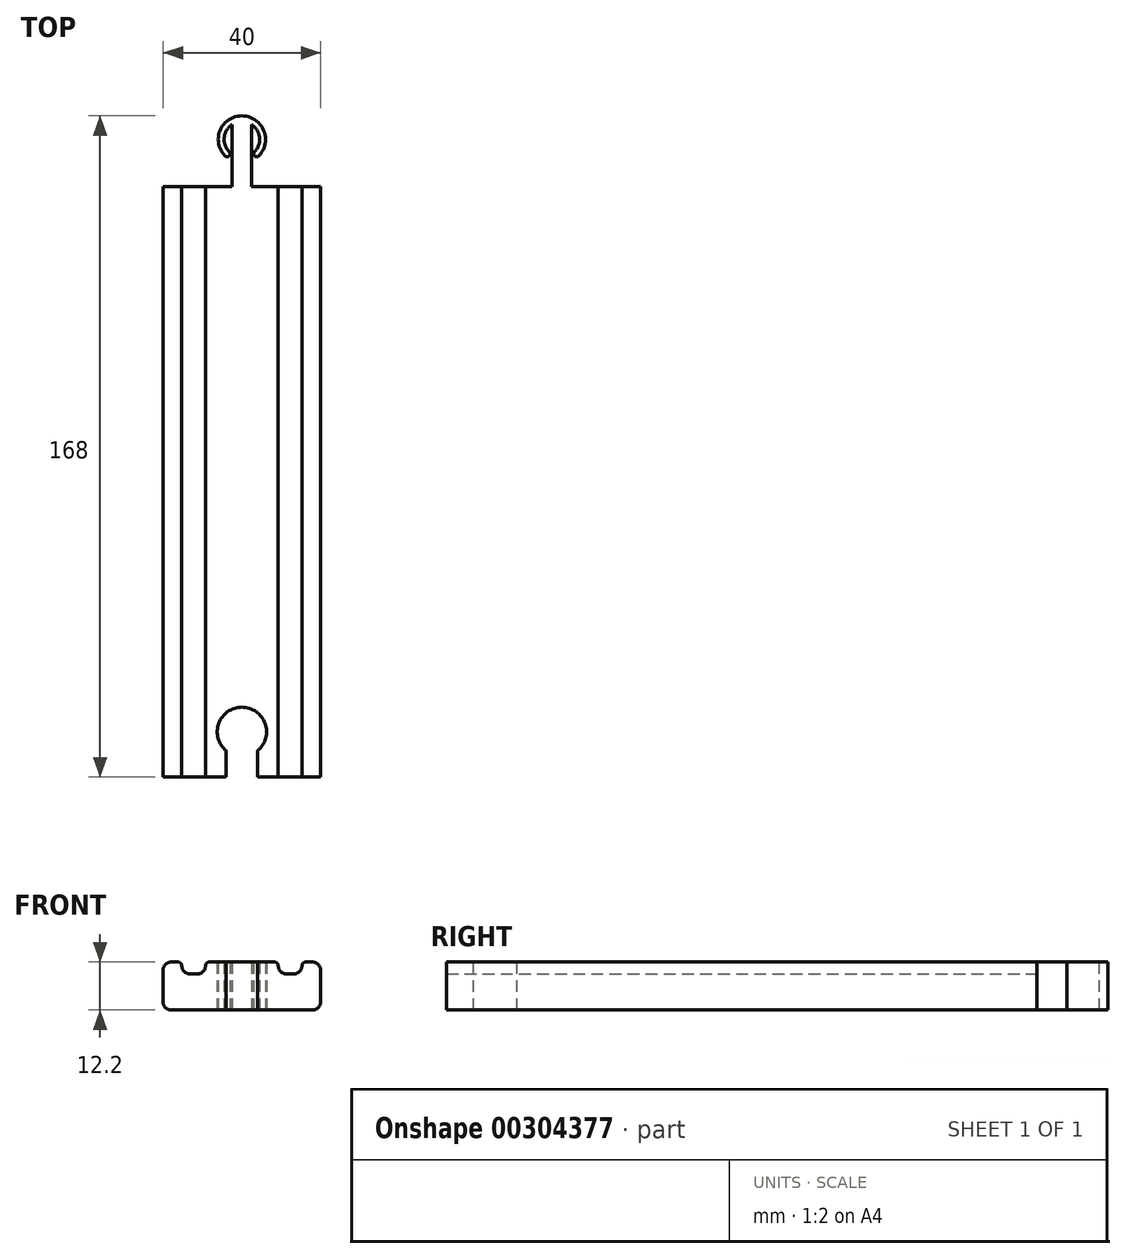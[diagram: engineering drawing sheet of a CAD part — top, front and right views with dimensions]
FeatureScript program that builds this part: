
annotation { "Feature Type Name" : "Feature", "Feature Type Description" : "" }
export const myFeature = defineFeature(function(context is Context, id is Id, definition is map)
    precondition{}
    {
        {
            var Q0;
            Q0=qCreatedBy(makeId("Front.planeOp"),FACE);
            var sketch = newSketch(context, id + "F0", { "sketchPlane" : qUnion([Q0])});
            skLineSegment(sketch, "E0.bottom", {"start": v(18, 6.1) * mm, "end": v(16.25, 6.1) * mm});
            skLineSegment(sketch, "E0.top", {"start": v(18, -6.1) * mm, "end": v(-18, -6.1) * mm});
            skLineSegment(sketch, "E0.left", {"start": v(20, 4.1) * mm, "end": v(20, -4.1) * mm});
            skLineSegment(sketch, "E0.right", {"start": v(-20, 4.1) * mm, "end": v(-20, -4.1) * mm});
            skPoint(sketch, "E0.middle", {"position": v(0, 0) * mm});
            skPoint(sketch, "E1.visualSharp", {"position": v(-20, 6.1) * mm});
            skArc(sketch, "E1.filletArc", {"start": v(-18, 6.1) * mm, "mid": v(-19.41, 5.51) * mm, "end": v(-20, 4.1) * mm});
            skPoint(sketch, "E2.visualSharp", {"position": v(-20, -6.1) * mm});
            skArc(sketch, "E2.filletArc", {"start": v(-20, -4.1) * mm, "mid": v(-19.41, -5.51) * mm, "end": v(-18, -6.1) * mm});
            skPoint(sketch, "E3.visualSharp", {"position": v(20, -6.1) * mm});
            skArc(sketch, "E3.filletArc", {"start": v(18, -6.1) * mm, "mid": v(19.41, -5.51) * mm, "end": v(20, -4.1) * mm});
            skPoint(sketch, "E4.visualSharp", {"position": v(20, 6.1) * mm});
            skArc(sketch, "E4.filletArc", {"start": v(20, 4.1) * mm, "mid": v(19.41, 5.51) * mm, "end": v(18, 6.1) * mm});
            skLineSegment(sketch, "E5", {"start": v(0, 0) * mm, "end": v(0, 6.1) * mm, "construction": true});
            skLineSegment(sketch, "E6.top", {"start": v(9.25, 3.1) * mm, "end": v(15.25, 3.1) * mm});
            skLineSegment(sketch, "E6.left", {"start": v(9.25, 5.1) * mm, "end": v(9.25, 3.1) * mm});
            skLineSegment(sketch, "E6.right", {"start": v(15.25, 5.1) * mm, "end": v(15.25, 3.1) * mm});
            skLineSegment(sketch, "E7.MirrorCS", {"start": v(-15.25, 5.1) * mm, "end": v(-15.25, 3.1) * mm});
            skLineSegment(sketch, "E8.MirrorCS", {"start": v(-9.25, 5.1) * mm, "end": v(-9.25, 3.1) * mm});
            skLineSegment(sketch, "E9.MirrorCS", {"start": v(-9.25, 3.1) * mm, "end": v(-15.25, 3.1) * mm});
            skLineSegment(sketch, "E10.trimOffspring", {"start": v(-16.25, 6.1) * mm, "end": v(-18, 6.1) * mm});
            skLineSegment(sketch, "E11.trimOffspring", {"start": v(8.25, 6.1) * mm, "end": v(-8.25, 6.1) * mm});
            skPoint(sketch, "E12.visualSharp", {"position": v(-15.25, 6.1) * mm});
            skArc(sketch, "E12.filletArc", {"start": v(-15.25, 5.1) * mm, "mid": v(-15.54, 5.8) * mm, "end": v(-16.25, 6.1) * mm});
            skPoint(sketch, "E13.visualSharp", {"position": v(-9.25, 6.1) * mm});
            skArc(sketch, "E13.filletArc", {"start": v(-8.25, 6.1) * mm, "mid": v(-8.96, 5.8) * mm, "end": v(-9.25, 5.1) * mm});
            skPoint(sketch, "E14.visualSharp", {"position": v(9.25, 6.1) * mm});
            skArc(sketch, "E14.filletArc", {"start": v(9.25, 5.1) * mm, "mid": v(8.96, 5.8) * mm, "end": v(8.25, 6.1) * mm});
            skPoint(sketch, "E15.visualSharp", {"position": v(15.25, 6.1) * mm});
            skArc(sketch, "E15.filletArc", {"start": v(16.25, 6.1) * mm, "mid": v(15.54, 5.8) * mm, "end": v(15.25, 5.1) * mm});
            skSolve(sketch);
        }
        {
            var Q0;
            Q0=makeQuery(id+"F0.imprint","IMPRINT",FACE,{"disambiguationData":[TD([[makeQuery(id+"F0.imprint","IMPRINT",EDGE,{"derivedFrom":sQuery(id+"F0.wireOp",EDGE,"E0.top")}),-1.0]])]});
            extrude(context, id + "F1", {"entities" : qUnion([Q0]), "depth" : 150 * mm});
        }
        {
            var Q0;
            Q0=makeQuery(id+"F1.opExtrude","SWEPT_EDGE",EDGE,{"disambiguationData":[OSD([sQuery(id+"F0.wireOp",EDGE,"E0.bottom"),sQuery(id+"F0.wireOp",EDGE,"E7.MirrorCS"),sQuery(id+"F0.wireOp",EDGE,"18113322-55e9-4600-aaab-a5ac58dff54d3.MirrorCS")])]});
            var Q1;
            Q1=makeQuery(id+"F1.opExtrude","SWEPT_EDGE",EDGE,{"disambiguationData":[OSD([sQuery(id+"F0.wireOp",EDGE,"E0.bottom"),sQuery(id+"F0.wireOp",EDGE,"E8.MirrorCS"),sQuery(id+"F0.wireOp",EDGE,"18113322-55e9-4600-aaab-a5ac58dff54d3.MirrorCS")])]});
            var Q2;
            Q2=makeQuery(id+"F1.opExtrude","SWEPT_EDGE",EDGE,{"disambiguationData":[OSD([sQuery(id+"F0.wireOp",EDGE,"E0.bottom"),sQuery(id+"F0.wireOp",EDGE,"E6.bottom"),sQuery(id+"F0.wireOp",EDGE,"E6.left")])]});
            var Q3;
            Q3=makeQuery(id+"F1.opExtrude","SWEPT_EDGE",EDGE,{"disambiguationData":[OSD([sQuery(id+"F0.wireOp",EDGE,"E0.bottom"),sQuery(id+"F0.wireOp",EDGE,"E6.bottom"),sQuery(id+"F0.wireOp",EDGE,"E6.right")])]});
            fillet(context, id + "F2", {"entities" : qUnion([Q0, Q1, Q2, Q3]), "radius" : 2 * mm, "tangentPropagation" : true, "allowEdgeOverflow" : false});
        }
        {
            var Q0;
            Q0=makeQuery(id+"F1.opExtrude","SWEPT_FACE",FACE,{"disambiguationData":[OSD([sQuery(id+"F0.wireOp",EDGE,"E0.top")])]});
            var sketch = newSketch(context, id + "F3", { "sketchPlane" : qUnion([Q0])});
            skCircle(sketch, "E16", {"center": v(0, 138.5) * mm, "radius": 6.25 * mm});
            skLineSegment(sketch, "E17", {"start": v(0, 138.5) * mm, "end": v(0, 150) * mm, "construction": true});
            skLineSegment(sketch, "E18", {"start": v(4, 143.3) * mm, "end": v(4, 150) * mm});
            skLineSegment(sketch, "E19.MirrorCS", {"start": v(-4, 143.3) * mm, "end": v(-4, 150) * mm});
            skLineSegment(sketch, "E20", {"start": v(0, 0) * mm, "end": v(0, -12) * mm});
            skPoint(sketch, "E20.endSnap0", {"position": v(0, 0) * mm});
            skCircle(sketch, "E21", {"center": v(0, -12) * mm, "radius": 6 * mm});
            skLineSegment(sketch, "E22", {"start": v(2.5, -6.55) * mm, "end": v(2.5, 0) * mm});
            skLineSegment(sketch, "E23.MirrorCS", {"start": v(-2.5, -6.55) * mm, "end": v(-2.5, 0) * mm});
            skCircle(sketch, "E24", {"center": v(0, -12) * mm, "radius": 4.5 * mm});
            skLineSegment(sketch, "E25", {"start": v(2.5, -6.55) * mm, "end": v(2.5, -15.74) * mm});
            skLineSegment(sketch, "E26", {"start": v(-2.5, -6.55) * mm, "end": v(-2.5, -15.74) * mm});
            skArc(sketch, "E27", {"start": v(-3.21, -8.85) * mm, "mid": v(-3.23, -7.8) * mm, "end": v(-4.29, -7.8) * mm});
            skArc(sketch, "E28.MirrorCS", {"start": v(3.21, -8.85) * mm, "mid": v(3.23, -7.8) * mm, "end": v(4.29, -7.8) * mm});
            skSolve(sketch);
        }
        {
            var Q0;
            {var subQ5=sQuery(id+"F3.wireOp",EDGE,"E23.MirrorCS");Q0=makeQuery(id+"F3.imprint","IMPRINT",FACE,{"disambiguationData":[TD([[makeQuery(id+"F3.imprint","IMPRINT",EDGE,{"derivedFrom":subQ5}),-1.0]])]});}
            var Q1;
            {var subQ5=sQuery(id+"F3.wireOp",EDGE,"E22");Q1=makeQuery(id+"F3.imprint","IMPRINT",FACE,{"disambiguationData":[TD([[makeQuery(id+"F3.imprint","IMPRINT",EDGE,{"derivedFrom":subQ5}),1.0]])]});}
            var Q2;
            {var subQ0=sQuery(id+"F3.wireOp",EDGE,"E24");var subQ1=sQuery(id+"F3.wireOp",EDGE,"E20");var subQ2=makeQuery(id+"F3.imprint","INTERSECT",VERTEX,{"derivedFrom":[subQ1,subQ0]});Q2=makeQuery(id+"F3.imprint","IMPRINT",FACE,{"disambiguationData":[TD([[makeQuery(id+"F3.imprint","IMPRINT",EDGE,{"disambiguationData":[TD([[subQ2,1.0]])],"derivedFrom":subQ1}),1.0]])]});}
            var Q3;
            {var subQ0=sQuery(id+"F3.wireOp",EDGE,"E24");var subQ1=sQuery(id+"F3.wireOp",EDGE,"E20");var subQ2=makeQuery(id+"F3.imprint","INTERSECT",VERTEX,{"derivedFrom":[subQ1,subQ0]});Q3=makeQuery(id+"F3.imprint","IMPRINT",FACE,{"disambiguationData":[TD([[makeQuery(id+"F3.imprint","IMPRINT",EDGE,{"disambiguationData":[TD([[subQ2,1.0]])],"derivedFrom":subQ1}),-1.0]])]});}
            var Q4;
            {var subQ1=sQuery(id+"F3.wireOp",EDGE,"E24");var subQ6=makeQuery(id+"F3.imprint","INTERSECT",VERTEX,{"derivedFrom":[sQuery(id+"F3.wireOp",EDGE,"E20"),subQ1]});Q4=makeQuery(id+"F3.imprint","IMPRINT",FACE,{"disambiguationData":[TD([[makeQuery(id+"F3.imprint","IMPRINT",EDGE,{"disambiguationData":[TD([[subQ6,1.0]])],"derivedFrom":subQ1}),1.0]])]});}
            var Q5;
            {var subQ4=sQuery(id+"F3.wireOp",EDGE,"E27");Q5=makeQuery(id+"F3.imprint","IMPRINT",FACE,{"disambiguationData":[TD([[makeQuery(id+"F3.imprint","IMPRINT",EDGE,{"derivedFrom":subQ4}),1.0]])]});}
            extrude(context, id + "F4", {"entities" : qUnion([Q0, Q1, Q2, Q3, Q4, Q5]), "operationType" : NewBodyOperationType.ADD, "oppositeDirection" : true, "depth" : 12.2 * mm});
        }
        {
            var Q0;
            {var subQ0=sQuery(id+"F3.wireOp",EDGE,"E18");Q0=makeQuery(id+"F3.imprint","IMPRINT",FACE,{"disambiguationData":[TD([[makeQuery(id+"F3.imprint","IMPRINT",EDGE,{"derivedFrom":subQ0}),1.0]])]});}
            var Q1;
            {var subQ0=sQuery(id+"F3.wireOp",EDGE,"E16");var subQ1=makeQuery(id+"F3.imprint","INTERSECT",VERTEX,{"derivedFrom":[subQ0,sQuery(id+"F3.wireOp",EDGE,"E18")]});Q1=makeQuery(id+"F3.imprint","IMPRINT",FACE,{"disambiguationData":[TD([[makeQuery(id+"F3.imprint","IMPRINT",EDGE,{"disambiguationData":[TD([[subQ1,-1.0]])],"derivedFrom":subQ0}),1.0]])]});}
            extrude(context, id + "F5", {"entities" : qUnion([Q0, Q1]), "operationType" : NewBodyOperationType.REMOVE, "oppositeDirection" : true, "depth" : 25 * mm});
        }
    });
